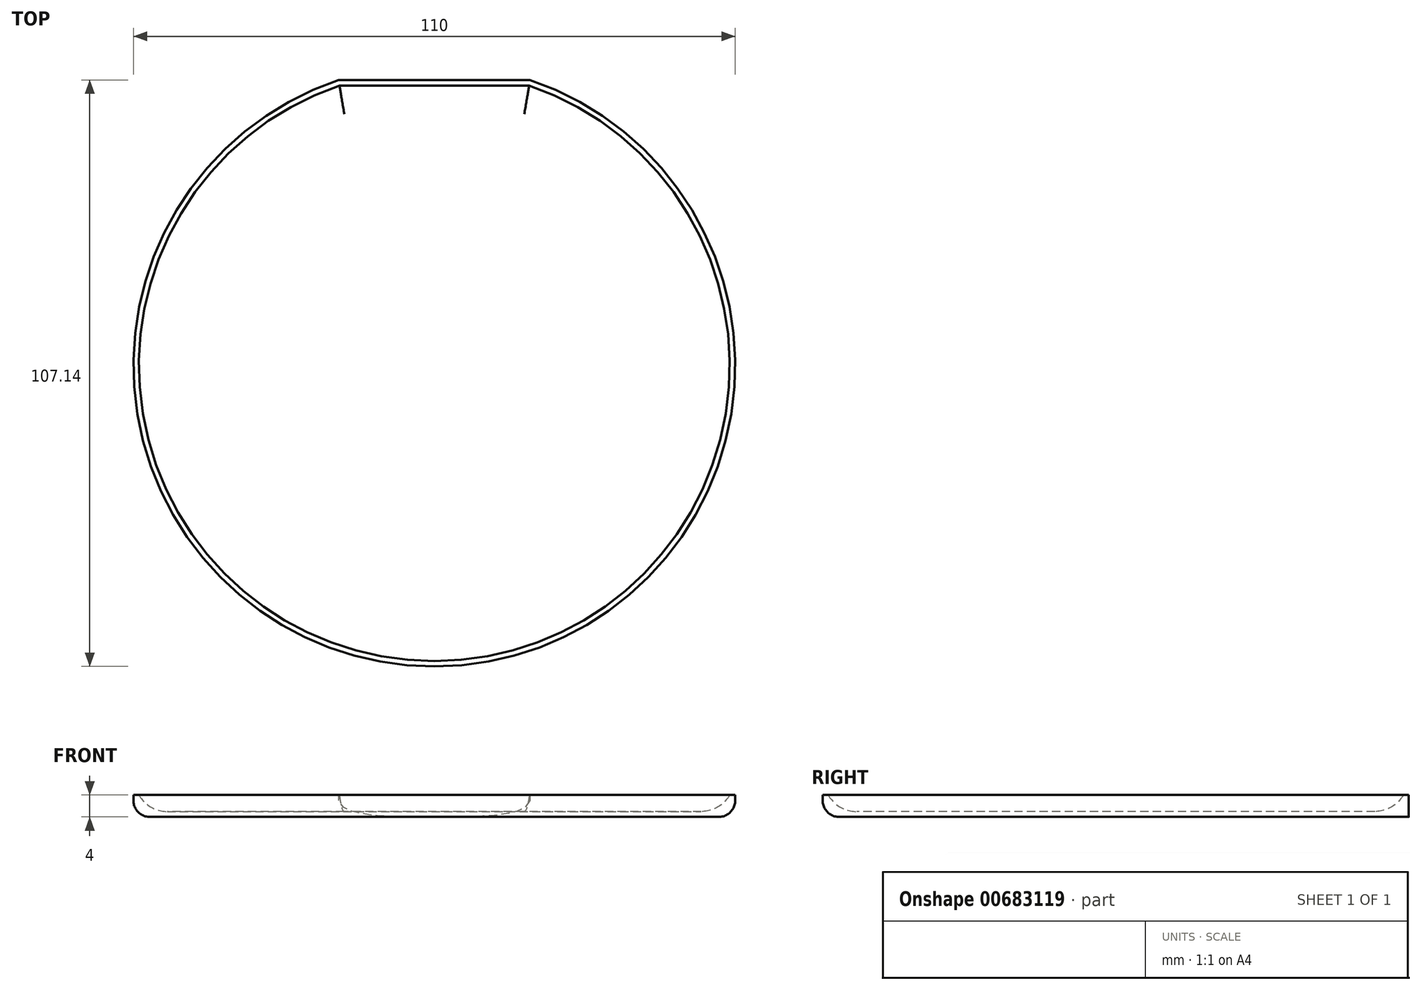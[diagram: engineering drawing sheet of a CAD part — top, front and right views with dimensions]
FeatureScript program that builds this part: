
annotation { "Feature Type Name" : "Feature", "Feature Type Description" : "" }
export const myFeature = defineFeature(function(context is Context, id is Id, definition is map)
    precondition{}
    {
        {
            var Q0;
            Q0=qCreatedBy(makeId("Top.planeOp"),FACE);
            var sketch = newSketch(context, id + "F0", { "sketchPlane" : qUnion([Q0])});
            skArc(sketch, "E0", {"start": v(-17.5, 52.14) * mm, "mid": v(0, -55) * mm, "end": v(17.5, 52.14) * mm});
            skLineSegment(sketch, "E1", {"start": v(-17.5, 52.14) * mm, "end": v(17.5, 52.14) * mm});
            skSolve(sketch);
        }
        {
            var Q0;
            Q0=qSketchRegion(id+"F0",true);
            extrude(context, id + "F1", {"entities" : qUnion([Q0]), "depth" : 4 * mm, "offsetDistance" : 25.4 * mm});
        }
        {
            var Q0;
            Q0=makeQuery(id+"F1.opExtrude","CAP_FACE",FACE,{"disambiguationData":[OSD([sQuery(id+"F0.wireOp",EDGE,"3EveOp2L-82Nq-lBtr-bmo9-LZEQdsZC4kzb.bottom"),sQuery(id+"F0.wireOp",EDGE,"3EveOp2L-82Nq-lBtr-bmo9-LZEQdsZC4kzb.top"),sQuery(id+"F0.wireOp",EDGE,"3EveOp2L-82Nq-lBtr-bmo9-LZEQdsZC4kzb.left"),sQuery(id+"F0.wireOp",EDGE,"3EveOp2L-82Nq-lBtr-bmo9-LZEQdsZC4kzb.right")])],"isStart":false});
            var Q1;
            Q1=makeQuery(id+"F1.opExtrude","CAP_FACE",FACE,{"disambiguationData":[OSD([sQuery(id+"F0.wireOp",EDGE,"E0"),sQuery(id+"F0.wireOp",EDGE,"E1")])],"isStart":false});
            shell(context, id + "F2", {"entities" : qUnion([Q0, Q1]), "thickness" : 1 * mm});
        }
        {
            var Q0;
            Q0=makeQuery(id+"F2.opShell","OFFSET_FACE",FACE,{"disambiguationData":[OSD([sQuery(id+"F0.wireOp",EDGE,"E0"),sQuery(id+"F0.wireOp",EDGE,"E1")])]});
            fillet(context, id + "F3", {"entities" : qUnion([Q0]), "radius" : 6 * mm, "tangentPropagation" : true, "allowEdgeOverflow" : false});
        }
        {
            var Q0;
            Q0=makeQuery(id+"F1.opExtrude","CAP_EDGE",EDGE,{"disambiguationData":[OSD([sQuery(id+"F0.wireOp",EDGE,"E0")])],"isStart":true});
            fillet(context, id + "F4", {"entities" : qUnion([Q0]), "radius" : 3 * mm, "tangentPropagation" : true, "allowEdgeOverflow" : false});
        }
    });
